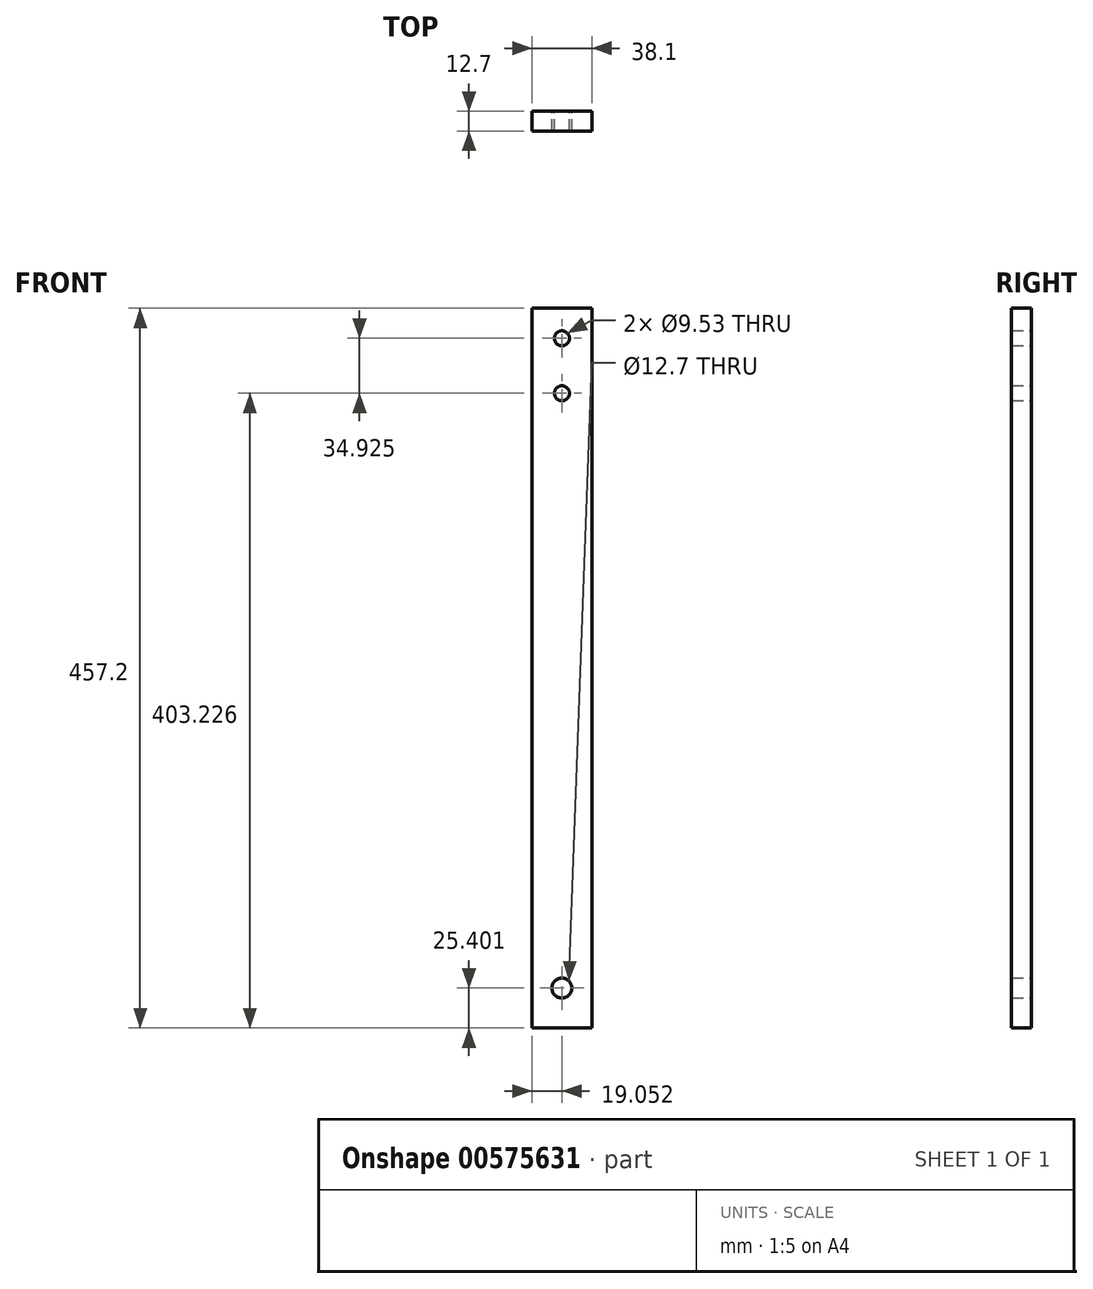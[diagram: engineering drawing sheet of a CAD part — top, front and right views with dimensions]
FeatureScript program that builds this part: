
annotation { "Feature Type Name" : "Feature", "Feature Type Description" : "" }
export const myFeature = defineFeature(function(context is Context, id is Id, definition is map)
    precondition{}
    {
        {
            var Q0;
            Q0=qCreatedBy(makeId("Front.planeOp"),FACE);
            var sketch = newSketch(context, id + "F0", { "sketchPlane" : qUnion([Q0])});
            skLineSegment(sketch, "E0.bottom", {"start": v(-23.72, 429.74) * mm, "end": v(14.38, 429.74) * mm});
            skLineSegment(sketch, "E0.top", {"start": v(-23.72, -27.46) * mm, "end": v(14.38, -27.46) * mm});
            skLineSegment(sketch, "E0.left", {"start": v(-23.72, 429.74) * mm, "end": v(-23.72, -27.46) * mm});
            skLineSegment(sketch, "E0.right", {"start": v(14.38, 429.74) * mm, "end": v(14.38, -27.46) * mm});
            skCircle(sketch, "E1", {"center": v(-4.67, -2.06) * mm, "radius": 6.35 * mm});
            skCircle(sketch, "E2", {"center": v(-4.67, 410.7) * mm, "radius": 4.76 * mm});
            skCircle(sketch, "E3", {"center": v(-4.67, 375.77) * mm, "radius": 4.76 * mm});
            skLineSegment(sketch, "E4", {"start": v(-4.67, 410.7) * mm, "end": v(-4.67, 429.74) * mm});
            skLineSegment(sketch, "E5", {"start": v(-4.67, 410.7) * mm, "end": v(-4.67, 375.77) * mm});
            skLineSegment(sketch, "E6", {"start": v(-4.67, -2.06) * mm, "end": v(-4.67, -27.46) * mm});
            skSolve(sketch);
        }
        {
            var Q0;
            Q0=qSketchRegion(id+"F0",true);
            extrude(context, id + "F1", {"entities" : qUnion([Q0]), "depth" : 12.7 * mm, "offsetDistance" : 25.4 * mm});
        }
    });
